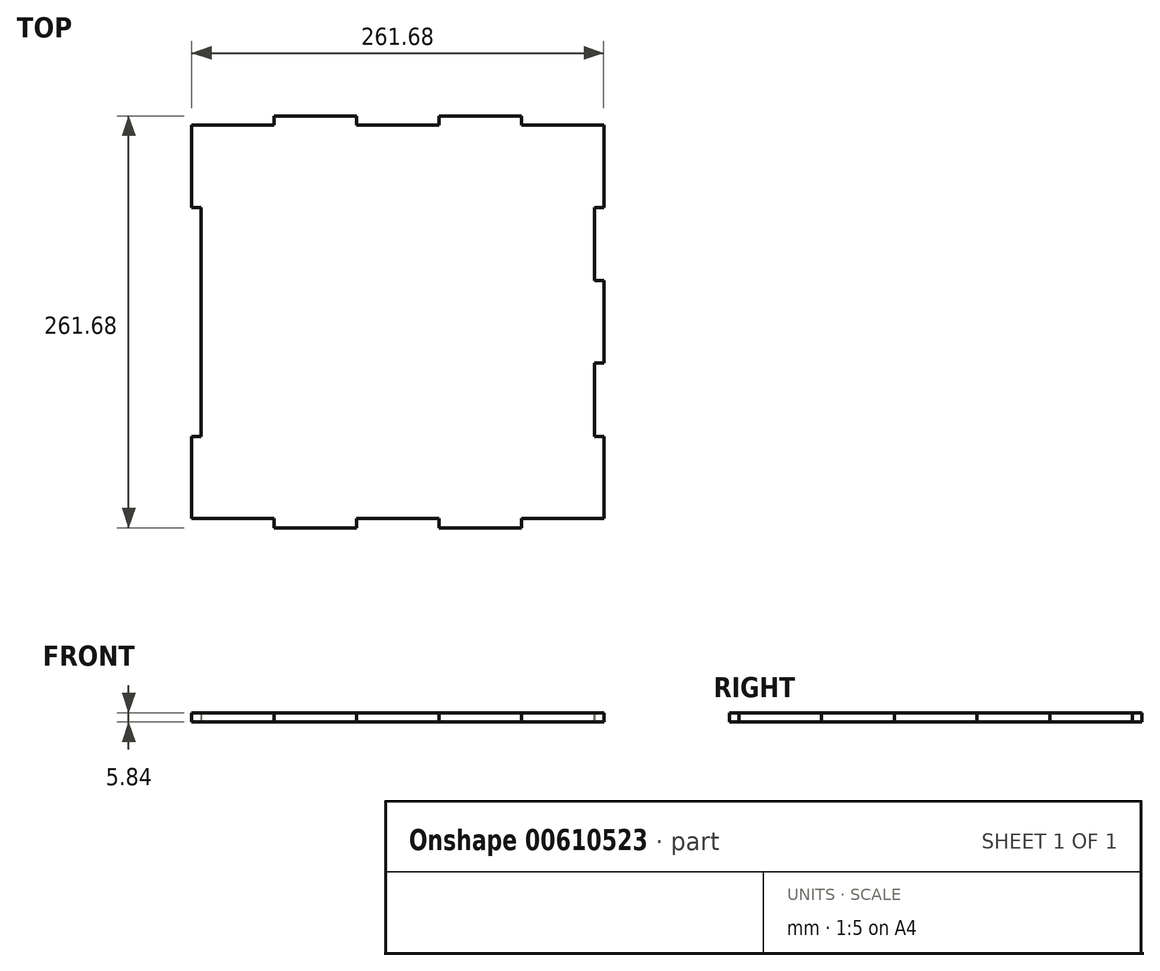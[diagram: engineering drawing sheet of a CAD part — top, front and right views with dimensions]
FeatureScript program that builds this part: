
annotation { "Feature Type Name" : "Feature", "Feature Type Description" : "" }
export const myFeature = defineFeature(function(context is Context, id is Id, definition is map)
    precondition{}
    {
        {
            var Q0;
            Q0=qCreatedBy(makeId("Top.planeOp"),FACE);
            var sketch = newSketch(context, id + "F0", { "sketchPlane" : qUnion([Q0])});
            skLineSegment(sketch, "E0.bottom", {"start": v(125, 125) * mm, "end": v(-125, 125) * mm});
            skLineSegment(sketch, "E0.top", {"start": v(125, -125) * mm, "end": v(-125, -125) * mm});
            skLineSegment(sketch, "E0.left", {"start": v(125, 125) * mm, "end": v(125, -125) * mm});
            skLineSegment(sketch, "E0.right", {"start": v(-125, 125) * mm, "end": v(-125, -125) * mm});
            skPoint(sketch, "E0.middle", {"position": v(0, 0) * mm});
            skLineSegment(sketch, "E1.top", {"start": v(-78.5, -130.84) * mm, "end": v(-26.17, -130.84) * mm});
            skLineSegment(sketch, "E2.bottom", {"start": v(-26.17, 125) * mm, "end": v(26.17, 125) * mm});
            skLineSegment(sketch, "E2.left", {"start": v(-26.17, 125) * mm, "end": v(-26.17, 130.84) * mm});
            skLineSegment(sketch, "E2.right", {"start": v(26.17, 125) * mm, "end": v(26.17, 130.84) * mm});
            skLineSegment(sketch, "E3.bottom", {"start": v(-78.5, 125) * mm, "end": v(-26.17, 125) * mm});
            skLineSegment(sketch, "E3.top", {"start": v(-78.5, 130.84) * mm, "end": v(-26.17, 130.84) * mm});
            skLineSegment(sketch, "E3.left", {"start": v(-78.5, 125) * mm, "end": v(-78.5, 130.84) * mm});
            skLineSegment(sketch, "E4.top", {"start": v(-125, 125) * mm, "end": v(-78.5, 125) * mm});
            skLineSegment(sketch, "E4.right", {"start": v(-78.5, 130.84) * mm, "end": v(-78.5, 125) * mm});
            skLineSegment(sketch, "E5.bottom", {"start": v(26.17, 130.84) * mm, "end": v(78.5, 130.84) * mm});
            skLineSegment(sketch, "E5.top", {"start": v(26.17, 125) * mm, "end": v(78.5, 125) * mm});
            skLineSegment(sketch, "E5.left", {"start": v(26.17, 130.84) * mm, "end": v(26.17, 125) * mm});
            skLineSegment(sketch, "E5.right", {"start": v(78.5, 130.84) * mm, "end": v(78.5, 125) * mm});
            skLineSegment(sketch, "E6.top", {"start": v(78.5, 125) * mm, "end": v(125, 125) * mm});
            skLineSegment(sketch, "E7.left", {"start": v(-125, 72.66) * mm, "end": v(-125, 26.17) * mm});
            skLineSegment(sketch, "E8.right", {"start": v(-125, 125) * mm, "end": v(-125, 72.66) * mm});
            skLineSegment(sketch, "E9.right", {"start": v(-125, -125) * mm, "end": v(-125, -72.66) * mm});
            skLineSegment(sketch, "E10.top", {"start": v(-26.17, -125) * mm, "end": v(26.17, -125) * mm});
            skLineSegment(sketch, "E10.left", {"start": v(-26.17, -130.84) * mm, "end": v(-26.17, -125) * mm});
            skLineSegment(sketch, "E10.right", {"start": v(26.17, -130.84) * mm, "end": v(26.17, -125) * mm});
            skLineSegment(sketch, "E11.bottom", {"start": v(-26.17, -130.84) * mm, "end": v(-78.5, -130.84) * mm});
            skLineSegment(sketch, "E11.top", {"start": v(-26.17, -125) * mm, "end": v(-78.5, -125) * mm});
            skLineSegment(sketch, "E11.right", {"start": v(-78.5, -130.84) * mm, "end": v(-78.5, -125) * mm});
            skLineSegment(sketch, "E12.top", {"start": v(-78.5, -125) * mm, "end": v(-125, -125) * mm});
            skLineSegment(sketch, "E13.bottom", {"start": v(26.17, -130.84) * mm, "end": v(78.5, -130.84) * mm});
            skLineSegment(sketch, "E13.top", {"start": v(26.17, -125) * mm, "end": v(78.5, -125) * mm});
            skLineSegment(sketch, "E13.right", {"start": v(78.5, -130.84) * mm, "end": v(78.5, -125) * mm});
            skLineSegment(sketch, "E14.top", {"start": v(78.5, -125) * mm, "end": v(125, -125) * mm});
            skLineSegment(sketch, "E15.right", {"start": v(125, -125) * mm, "end": v(125, -72.66) * mm});
            skLineSegment(sketch, "E16.right", {"start": v(125, -72.66) * mm, "end": v(125, -26.17) * mm});
            skLineSegment(sketch, "E17.left", {"start": v(125, -26.17) * mm, "end": v(125, 26.17) * mm});
            skLineSegment(sketch, "E18.left", {"start": v(125, 26.17) * mm, "end": v(125, 72.66) * mm});
            skLineSegment(sketch, "E19.left", {"start": v(125, 72.66) * mm, "end": v(125, 125) * mm});
            skPoint(sketch, "E20.orphan", {"position": v(-130.84, 130.84) * mm});
            skPoint(sketch, "E21.trimOffspring.start.orphan", {"position": v(-130.84, -125) * mm});
            skPoint(sketch, "E9.bottom.start.orphan", {"position": v(-130.84, -130.84) * mm});
            skPoint(sketch, "E22.orphan", {"position": v(130.84, -130.84) * mm});
            skPoint(sketch, "E23.orphan", {"position": v(130.84, -125) * mm});
            skPoint(sketch, "E19.right.end.orphan", {"position": v(130.84, 130.84) * mm});
            skLineSegment(sketch, "E24.bottom", {"start": v(130.84, -125) * mm, "end": v(125, -125) * mm});
            skLineSegment(sketch, "E24.top", {"start": v(130.84, -72.66) * mm, "end": v(125, -72.66) * mm});
            skLineSegment(sketch, "E24.left", {"start": v(130.84, -125) * mm, "end": v(130.84, -72.66) * mm});
            skLineSegment(sketch, "E25.bottom", {"start": v(130.84, -26.17) * mm, "end": v(125, -26.17) * mm});
            skLineSegment(sketch, "E25.top", {"start": v(130.84, 26.17) * mm, "end": v(125, 26.17) * mm});
            skLineSegment(sketch, "E25.left", {"start": v(130.84, -26.17) * mm, "end": v(130.84, 26.17) * mm});
            skLineSegment(sketch, "E26.bottom", {"start": v(130.84, 72.66) * mm, "end": v(125, 72.66) * mm});
            skLineSegment(sketch, "E26.top", {"start": v(130.84, 125) * mm, "end": v(125, 125) * mm});
            skLineSegment(sketch, "E26.left", {"start": v(130.84, 72.66) * mm, "end": v(130.84, 125) * mm});
            skLineSegment(sketch, "E27.bottom", {"start": v(-130.84, -72.66) * mm, "end": v(-125, -72.66) * mm});
            skLineSegment(sketch, "E27.top", {"start": v(-130.84, -125) * mm, "end": v(-125, -125) * mm});
            skLineSegment(sketch, "E27.left", {"start": v(-130.84, -72.66) * mm, "end": v(-130.84, -125) * mm});
            skLineSegment(sketch, "E27.right", {"start": v(-125, -72.66) * mm, "end": v(-125, -125) * mm});
            skLineSegment(sketch, "E28.bottom", {"start": v(-130.84, -26.17) * mm, "end": v(-125, -26.17) * mm});
            skLineSegment(sketch, "E28.top", {"start": v(-130.84, 26.17) * mm, "end": v(-125, 26.17) * mm});
            skLineSegment(sketch, "E28.left", {"start": v(-130.84, -26.17) * mm, "end": v(-130.84, 26.17) * mm});
            skLineSegment(sketch, "E29.bottom", {"start": v(-130.84, 72.66) * mm, "end": v(-125, 72.66) * mm});
            skLineSegment(sketch, "E29.top", {"start": v(-130.84, 125) * mm, "end": v(-125, 125) * mm});
            skLineSegment(sketch, "E29.left", {"start": v(-130.84, 72.66) * mm, "end": v(-130.84, 125) * mm});
            skLineSegment(sketch, "E29.right", {"start": v(-125, 72.66) * mm, "end": v(-125, 125) * mm});
            skSolve(sketch);
        }
        {
            var Q0;
            Q0=qSketchRegion(id+"F0",true);
            extrude(context, id + "F1", {"entities" : qUnion([Q0]), "depth" : 5.84 * mm, "offsetDistance" : 25 * mm});
        }
    });
